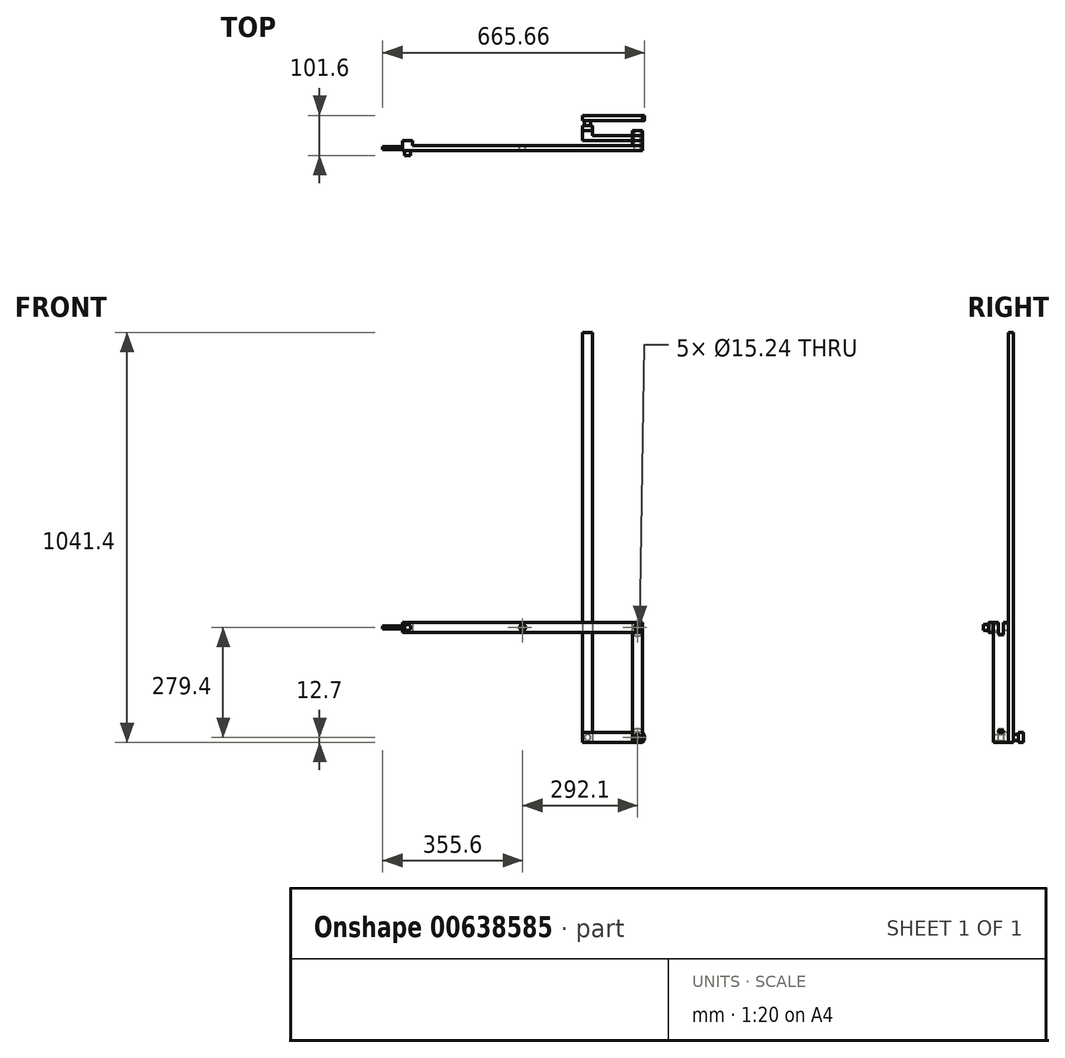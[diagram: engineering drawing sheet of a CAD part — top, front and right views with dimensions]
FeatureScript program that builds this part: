
annotation { "Feature Type Name" : "Feature", "Feature Type Description" : "" }
export const myFeature = defineFeature(function(context is Context, id is Id, definition is map)
    precondition{}
    {
        {
            var Q0;
            Q0=qCreatedBy(makeId("Front.planeOp"),FACE);
            var sketch = newSketch(context, id + "F0", { "sketchPlane" : qUnion([Q0])});
            skLineSegment(sketch, "E0.bottom", {"start": v(76.2, -12.7) * mm, "end": v(-76.2, -12.7) * mm});
            skLineSegment(sketch, "E0.top", {"start": v(76.2, 12.7) * mm, "end": v(-76.2, 12.7) * mm});
            skLineSegment(sketch, "E0.left", {"start": v(76.2, -12.7) * mm, "end": v(76.2, 12.7) * mm});
            skLineSegment(sketch, "E0.right", {"start": v(-76.2, -12.7) * mm, "end": v(-76.2, 12.7) * mm});
            skPoint(sketch, "E0.middle", {"position": v(0, 0) * mm});
            skCircle(sketch, "E1", {"center": v(-63.5, 0) * mm, "radius": 7.62 * mm});
            skLineSegment(sketch, "E2", {"start": v(-63.5, 0) * mm, "end": v(-63.5, 12.7) * mm, "construction": true});
            skLineSegment(sketch, "E3", {"start": v(-63.5, 0) * mm, "end": v(-76.2, 0) * mm, "construction": true});
            skCircle(sketch, "E4", {"center": v(63.5, 0) * mm, "radius": 7.62 * mm});
            skPoint(sketch, "E4.centerSnap0", {"position": v(76.2, 0) * mm});
            skLineSegment(sketch, "E5", {"start": v(63.5, 0) * mm, "end": v(76.2, 0) * mm, "construction": true});
            skSolve(sketch);
        }
        {
            var Q0;
            Q0=makeQuery(id+"F0.imprint","IMPRINT",FACE,{"disambiguationData":[TD([[makeQuery(id+"F0.imprint","IMPRINT",EDGE,{"derivedFrom":sQuery(id+"F0.wireOp",EDGE,"E0.bottom")}),-1.0]])]});
            extrude(context, id + "F1", {"entities" : qUnion([Q0]), "endBound" : BoundingType.SYMMETRIC, "depth" : 12.7 * mm, "offsetDistance" : 25.4 * mm});
        }
        {
            var Q0;
            Q0=makeQuery(id+"F1.opExtrude","CAP_FACE",FACE,{"disambiguationData":[OSD([sQuery(id+"F0.wireOp",EDGE,"E0.bottom"),sQuery(id+"F0.wireOp",EDGE,"E0.top"),sQuery(id+"F0.wireOp",EDGE,"E0.left"),sQuery(id+"F0.wireOp",EDGE,"E0.right"),sQuery(id+"F0.wireOp",EDGE,"E1"),sQuery(id+"F0.wireOp",EDGE,"E4")])],"isStart":false});
            var sketch = newSketch(context, id + "F2", { "sketchPlane" : qUnion([Q0])});
            skLineSegment(sketch, "E6.bottom", {"start": v(76.2, -12.7) * mm, "end": v(50.8, -12.7) * mm});
            skLineSegment(sketch, "E6.top", {"start": v(76.2, 292.1) * mm, "end": v(50.8, 292.1) * mm});
            skLineSegment(sketch, "E6.left", {"start": v(76.2, -12.7) * mm, "end": v(76.2, 292.1) * mm});
            skLineSegment(sketch, "E6.right", {"start": v(50.8, -12.7) * mm, "end": v(50.8, 292.1) * mm});
            skLineSegment(sketch, "E7", {"start": v(63.5, 0) * mm, "end": v(63.5, -12.7) * mm, "construction": true});
            skLineSegment(sketch, "E8", {"start": v(76.2, 139.7) * mm, "end": v(50.8, 139.7) * mm, "construction": true});
            skCircle(sketch, "E9", {"center": v(63.5, 279.4) * mm, "radius": 7.62 * mm});
            skLineSegment(sketch, "E10", {"start": v(76.2, 12.7) * mm, "end": v(50.8, 12.7) * mm});
            skSolve(sketch);
        }
        {
            var Q0;
            {var subQ2=sQuery(id+"F2.wireOp",EDGE,"E6.bottom");Q0=makeQuery(id+"F2.imprint","IMPRINT",FACE,{"disambiguationData":[TD([[makeQuery(id+"F2.imprint","IMPRINT",EDGE,{"derivedFrom":subQ2}),-1.0]])]});}
            var Q1;
            {var subQ1=sQuery(id+"F2.wireOp",EDGE,"E6.top");Q1=makeQuery(id+"F2.imprint","IMPRINT",FACE,{"disambiguationData":[TD([[makeQuery(id+"F2.imprint","IMPRINT",EDGE,{"derivedFrom":subQ1}),1.0]])]});}
            extrude(context, id + "F3", {"entities" : qUnion([Q0, Q1]), "depth" : 12.7 * mm, "offsetDistance" : 25.4 * mm});
        }
        {
            var Q0;
            {var subQ1=sQuery(id+"F2.wireOp",EDGE,"E6.top");Q0=makeQuery(id+"F2.imprint","IMPRINT",FACE,{"disambiguationData":[TD([[makeQuery(id+"F2.imprint","IMPRINT",EDGE,{"derivedFrom":subQ1}),1.0]])]});}
            var sketch = newSketch(context, id + "F4", { "sketchPlane" : qUnion([Q0])});
            skLineSegment(sketch, "E11.0", {"start": v(50.8, -12.7) * mm, "end": v(50.8, 292.1) * mm});
            skCircle(sketch, "E12.0", {"center": v(63.5, 0) * mm, "radius": 7.62 * mm});
            skCircle(sketch, "E13.0", {"center": v(63.5, 279.4) * mm, "radius": 7.62 * mm});
            skLineSegment(sketch, "E14", {"start": v(50.8, -12.7) * mm, "end": v(76.2, -12.7) * mm});
            skLineSegment(sketch, "E15.0", {"start": v(76.2, 292.1) * mm, "end": v(50.8, 292.1) * mm});
            skPoint(sketch, "E16.orphan", {"position": v(-76.2, 12.7) * mm});
            skLineSegment(sketch, "E17.trimOffspring", {"start": v(76.2, -12.7) * mm, "end": v(76.2, 292.1) * mm});
            skLineSegment(sketch, "E18", {"start": v(50.8, 139.7) * mm, "end": v(76.2, 139.7) * mm, "construction": true});
            skArc(sketch, "E19", {"start": v(50.8, 261.62) * mm, "mid": v(63.5, 257.55) * mm, "end": v(76.2, 261.62) * mm});
            skArc(sketch, "E20", {"start": v(76.2, 17.78) * mm, "mid": v(63.5, 21.85) * mm, "end": v(50.8, 17.78) * mm});
            skSolve(sketch);
        }
        {
            var Q0;
            {var subQ0=sQuery(id+"F4.wireOp",EDGE,"E19");Q0=makeQuery(id+"F4.imprint","IMPRINT",FACE,{"disambiguationData":[TD([[makeQuery(id+"F4.imprint","IMPRINT",EDGE,{"derivedFrom":subQ0}),-1.0]])]});}
            var Q1;
            Q1=makeQuery(id+"F1.opExtrude","CAP_FACE",FACE,{"disambiguationData":[OSD([sQuery(id+"F0.wireOp",EDGE,"E0.bottom"),sQuery(id+"F0.wireOp",EDGE,"E0.top"),sQuery(id+"F0.wireOp",EDGE,"E0.left"),sQuery(id+"F0.wireOp",EDGE,"E0.right"),sQuery(id+"F0.wireOp",EDGE,"E1"),sQuery(id+"F0.wireOp",EDGE,"E4")])],"isStart":true});
            extrude(context, id + "F5", {"entities" : qUnion([Q0]), "operationType" : NewBodyOperationType.ADD, "endBound" : BoundingType.UP_TO_SURFACE, "oppositeDirection" : true, "depth" : 34.04 * mm, "endBoundEntityFace" : qUnion([Q1]), "offsetDistance" : 25.4 * mm});
        }
        {
            var Q0;
            Q0=makeQuery(id+"F5.opExtrude","CAP_FACE",FACE,{"disambiguationData":[OSD([sQuery(id+"F4.wireOp",EDGE,"E11.0"),sQuery(id+"F4.wireOp",EDGE,"E17.trimOffspring"),sQuery(id+"F4.wireOp",EDGE,"E19"),sQuery(id+"F4.wireOp",EDGE,"E20")])],"isStart":false});
            var sketch = newSketch(context, id + "F6", { "sketchPlane" : qUnion([Q0])});
            skLineSegment(sketch, "E21.0", {"start": v(-50.8, -12.7) * mm, "end": v(-50.8, 292.1) * mm});
            skLineSegment(sketch, "E22.0", {"start": v(-76.2, -12.7) * mm, "end": v(-76.2, 292.1) * mm});
            skLineSegment(sketch, "E23.0", {"start": v(-76.2, 292.1) * mm, "end": v(-50.8, 292.1) * mm});
            skCircle(sketch, "E24.0", {"center": v(-63.5, 279.4) * mm, "radius": 7.62 * mm});
            skCircle(sketch, "E25.0", {"center": v(-63.5, 0) * mm, "radius": 7.62 * mm});
            skLineSegment(sketch, "E26.0", {"start": v(-76.2, -12.7) * mm, "end": v(-50.8, -12.7) * mm});
            skSolve(sketch);
        }
        {
            var Q0;
            {var subQ1=makeQuery(id+"F5.opExtrude","CAP_EDGE",EDGE,{"disambiguationData":[OSD([sQuery(id+"F4.wireOp",EDGE,"E19")])],"isStart":false});Q0=makeQuery(id+"F6.imprint","IMPRINT",FACE,{"disambiguationData":[TD([[makeQuery(id+"F6.imprint","IMPRINT",EDGE,{"derivedFrom":subQ1}),-1.0]])]});}
            var Q1;
            Q1=makeQuery(id+"F6.imprint","IMPRINT",FACE,{"disambiguationData":[TD([[makeQuery(id+"F6.imprint","IMPRINT",EDGE,{"derivedFrom":sQuery(id+"F6.wireOp",EDGE,"E25.0")}),-1.0]])]});
            var Q2;
            {var subQ0=sQuery(id+"F6.wireOp",EDGE,"E23.0");Q2=makeQuery(id+"F6.imprint","IMPRINT",FACE,{"disambiguationData":[TD([[makeQuery(id+"F6.imprint","IMPRINT",EDGE,{"derivedFrom":subQ0}),-1.0]])]});}
            extrude(context, id + "F7", {"entities" : qUnion([Q0, Q1, Q2]), "operationType" : NewBodyOperationType.ADD, "depth" : 12.7 * mm, "offsetDistance" : 25.4 * mm});
        }
        {
            var Q0;
            Q0=makeQuery(id+"F3.opExtrude","CAP_FACE",FACE,{"disambiguationData":[OSD([sQuery(id+"F0.wireOp",EDGE,"E4"),sQuery(id+"F2.wireOp",EDGE,"E6.bottom"),sQuery(id+"F2.wireOp",EDGE,"E6.top"),sQuery(id+"F2.wireOp",EDGE,"E6.left"),sQuery(id+"F2.wireOp",EDGE,"E6.right"),sQuery(id+"F2.wireOp",EDGE,"E9")])],"isStart":false});
            var sketch = newSketch(context, id + "F8", { "sketchPlane" : qUnion([Q0])});
            skLineSegment(sketch, "E27.bottom", {"start": v(76.2, 292.1) * mm, "end": v(-533.4, 292.1) * mm});
            skLineSegment(sketch, "E27.top", {"start": v(76.2, 266.7) * mm, "end": v(-533.4, 266.7) * mm});
            skLineSegment(sketch, "E27.left", {"start": v(76.2, 292.1) * mm, "end": v(76.2, 266.7) * mm});
            skLineSegment(sketch, "E27.right", {"start": v(-533.4, 292.1) * mm, "end": v(-533.4, 266.7) * mm});
            skCircle(sketch, "E28.0", {"center": v(63.5, 279.4) * mm, "radius": 7.62 * mm});
            skLineSegment(sketch, "E29", {"start": v(-228.6, 266.7) * mm, "end": v(-228.6, 292.1) * mm, "construction": true});
            skCircle(sketch, "E30", {"center": v(-520.7, 279.4) * mm, "radius": 7.62 * mm});
            skCircle(sketch, "E31", {"center": v(-228.6, 279.4) * mm, "radius": 7.62 * mm});
            skSolve(sketch);
        }
        {
            var Q0;
            {var subQ0=sQuery(id+"F8.wireOp",EDGE,"E27.right");Q0=makeQuery(id+"F8.imprint","IMPRINT",FACE,{"disambiguationData":[TD([[makeQuery(id+"F8.imprint","IMPRINT",EDGE,{"derivedFrom":subQ0}),1.0]])]});}
            var Q1;
            {var subQ0=sQuery(id+"F8.wireOp",EDGE,"E27.left");Q1=makeQuery(id+"F8.imprint","IMPRINT",FACE,{"disambiguationData":[TD([[makeQuery(id+"F8.imprint","IMPRINT",EDGE,{"derivedFrom":subQ0}),1.0]])]});}
            extrude(context, id + "F9", {"entities" : qUnion([Q0, Q1]), "depth" : 12.7 * mm, "offsetDistance" : 25.4 * mm});
        }
        {
            var Q0;
            Q0=makeQuery(id+"F1.opExtrude","CAP_FACE",FACE,{"disambiguationData":[OSD([sQuery(id+"F0.wireOp",EDGE,"E0.bottom"),sQuery(id+"F0.wireOp",EDGE,"E0.top"),sQuery(id+"F0.wireOp",EDGE,"E0.left"),sQuery(id+"F0.wireOp",EDGE,"E0.right"),sQuery(id+"F0.wireOp",EDGE,"E1"),sQuery(id+"F0.wireOp",EDGE,"E4")])],"isStart":true});
            var sketch = newSketch(context, id + "F10", { "sketchPlane" : qUnion([Q0])});
            skLineSegment(sketch, "E32.bottom", {"start": v(76.2, 12.7) * mm, "end": v(50.8, 12.7) * mm});
            skLineSegment(sketch, "E32.top", {"start": v(76.2, -12.7) * mm, "end": v(50.8, -12.7) * mm});
            skLineSegment(sketch, "E32.left", {"start": v(76.2, 12.7) * mm, "end": v(76.2, -12.7) * mm});
            skLineSegment(sketch, "E32.right", {"start": v(50.8, 12.7) * mm, "end": v(50.8, -12.7) * mm});
            skPoint(sketch, "E32.middle", {"position": v(63.5, 0) * mm});
            skCircle(sketch, "E33.0", {"center": v(63.5, 0) * mm, "radius": 7.62 * mm});
            skSolve(sketch);
        }
        {
            var Q0;
            Q0=makeQuery(id+"F10.imprint","IMPRINT",FACE,{"disambiguationData":[TD([[makeQuery(id+"F10.imprint","IMPRINT",EDGE,{"derivedFrom":sQuery(id+"F10.wireOp",EDGE,"E33.0")}),-1.0]])]});
            extrude(context, id + "F11", {"entities" : qUnion([Q0]), "oppositeDirection" : true, "depth" : 25.4 * mm, "offsetDistance" : 25.4 * mm});
        }
        {
            var Q0;
            Q0=makeQuery(id+"F10.imprint","IMPRINT",FACE,{"disambiguationData":[TD([[makeQuery(id+"F10.imprint","IMPRINT",EDGE,{"derivedFrom":sQuery(id+"F10.wireOp",EDGE,"E33.0")}),-1.0]])]});
            var Q1;
            Q1=makeQuery(id+"F10.imprint","IMPRINT",FACE,{"disambiguationData":[TD([[makeQuery(id+"F10.imprint","IMPRINT",EDGE,{"derivedFrom":sQuery(id+"F10.wireOp",EDGE,"E32.bottom")}),-1.0]])]});
            extrude(context, id + "F12", {"entities" : qUnion([Q0, Q1]), "operationType" : NewBodyOperationType.ADD, "depth" : 25.4 * mm, "offsetDistance" : 25.4 * mm});
        }
        {
            var Q0;
            Q0=makeQuery(id+"F12.opExtrude","SWEPT_FACE",FACE,{"disambiguationData":[OSD([sQuery(id+"F10.wireOp",EDGE,"E32.bottom")])]});
            var sketch = newSketch(context, id + "F13", { "sketchPlane" : qUnion([Q0])});
            skLineSegment(sketch, "E34", {"start": v(-76.2, 19.05) * mm, "end": v(-50.8, 19.05) * mm});
            skSolve(sketch);
        }
        {
            var Q0;
            {var subQ0=sQuery(id+"F13.wireOp",EDGE,"E34");Q0=makeQuery(id+"F13.imprint","IMPRINT",FACE,{"disambiguationData":[TD([[makeQuery(id+"F13.imprint","IMPRINT",EDGE,{"derivedFrom":subQ0}),1.0]])]});}
            extrude(context, id + "F14", {"entities" : qUnion([Q0]), "operationType" : NewBodyOperationType.ADD, "depth" : 889 * mm, "offsetDistance" : 25.4 * mm});
        }
        {
            var Q0;
            Q0=makeQuery(id+"F9.opExtrude","CAP_FACE",FACE,{"disambiguationData":[OSD([sQuery(id+"F8.wireOp",EDGE,"E27.bottom"),sQuery(id+"F8.wireOp",EDGE,"E27.top"),sQuery(id+"F8.wireOp",EDGE,"E27.left"),sQuery(id+"F8.wireOp",EDGE,"E27.right"),sQuery(id+"F8.wireOp",EDGE,"E28.0"),sQuery(id+"F8.wireOp",EDGE,"E30")])],"isStart":true});
            var sketch = newSketch(context, id + "F15", { "sketchPlane" : qUnion([Q0])});
            skLineSegment(sketch, "E35.bottom", {"start": v(533.4, 292.1) * mm, "end": v(508, 292.1) * mm});
            skLineSegment(sketch, "E35.top", {"start": v(533.4, 266.7) * mm, "end": v(508, 266.7) * mm});
            skLineSegment(sketch, "E35.left", {"start": v(533.4, 292.1) * mm, "end": v(533.4, 266.7) * mm});
            skLineSegment(sketch, "E35.right", {"start": v(508, 292.1) * mm, "end": v(508, 266.7) * mm});
            skPoint(sketch, "E35.middle", {"position": v(520.7, 279.4) * mm});
            skCircle(sketch, "E36.0", {"center": v(520.7, 279.4) * mm, "radius": 7.62 * mm});
            skSolve(sketch);
        }
        {
            var Q0;
            Q0=makeQuery(id+"F15.imprint","IMPRINT",FACE,{"disambiguationData":[TD([[makeQuery(id+"F15.imprint","IMPRINT",EDGE,{"derivedFrom":sQuery(id+"F15.wireOp",EDGE,"E36.0")}),-1.0]])]});
            var Q1;
            Q1=makeQuery(id+"F15.imprint","IMPRINT",FACE,{"disambiguationData":[TD([[makeQuery(id+"F15.imprint","IMPRINT",EDGE,{"derivedFrom":sQuery(id+"F15.wireOp",EDGE,"E35.bottom")}),-1.0]])]});
            extrude(context, id + "F16", {"entities" : qUnion([Q0, Q1]), "depth" : 12.7 * mm, "offsetDistance" : 25.4 * mm});
        }
        {
            var Q0;
            Q0=makeQuery(id+"F15.imprint","IMPRINT",FACE,{"disambiguationData":[TD([[makeQuery(id+"F15.imprint","IMPRINT",EDGE,{"derivedFrom":sQuery(id+"F15.wireOp",EDGE,"E36.0")}),-1.0]])]});
            extrude(context, id + "F17", {"entities" : qUnion([Q0]), "operationType" : NewBodyOperationType.ADD, "oppositeDirection" : true, "depth" : 25.4 * mm, "offsetDistance" : 25.4 * mm});
        }
        {
            var Q0;
            Q0=makeQuery(id+"F14.opExtrude","CAP_FACE",FACE,{"disambiguationData":[OSD([sQuery(id+"F0.wireOp",EDGE,"E0.top"),sQuery(id+"F10.wireOp",EDGE,"E32.bottom"),sQuery(id+"F10.wireOp",EDGE,"E32.left"),sQuery(id+"F10.wireOp",EDGE,"E32.right"),sQuery(id+"F13.wireOp",EDGE,"E34")])],"isStart":false});
            extrude(context, id + "F18", {"entities" : qUnion([Q0]), "operationType" : NewBodyOperationType.ADD, "depth" : 127 * mm, "offsetDistance" : 25.4 * mm});
        }
        {
            var Q0;
            Q0=makeQuery(id+"F9.opExtrude","SWEPT_FACE",FACE,{"disambiguationData":[OSD([sQuery(id+"F8.wireOp",EDGE,"E27.right")])]});
            var sketch = newSketch(context, id + "F19", { "sketchPlane" : qUnion([Q0])});
            skCircle(sketch, "E37", {"center": v(25.4, 279.4) * mm, "radius": 3.81 * mm});
            skPoint(sketch, "E37.centerSnap0", {"position": v(31.75, 279.4) * mm});
            skPoint(sketch, "E37.centerSnap1", {"position": v(25.4, 292.1) * mm});
            skSolve(sketch);
        }
        {
            var Q0;
            Q0=makeQuery(id+"F19.imprint","IMPRINT",FACE,{"disambiguationData":[TD([[makeQuery(id+"F19.imprint","IMPRINT",EDGE,{"derivedFrom":sQuery(id+"F19.wireOp",EDGE,"E37")}),1.0]])]});
            extrude(context, id + "F20", {"entities" : qUnion([Q0]), "operationType" : NewBodyOperationType.ADD, "depth" : 50.8 * mm, "offsetDistance" : 25.4 * mm});
        }
        {
            var Q0;
            Q0=makeQuery(id+"F11.opExtrude","CAP_FACE",FACE,{"disambiguationData":[OSD([sQuery(id+"F10.wireOp",EDGE,"E33.0")])],"isStart":false});
            extrude(context, id + "F21", {"entities" : qUnion([Q0]), "operationType" : NewBodyOperationType.REMOVE, "oppositeDirection" : true, "depth" : 65.02 * mm, "offsetDistance" : 25.4 * mm});
        }
        {
            var Q0;
            Q0=makeQuery(id+"F1.opExtrude","CAP_FACE",FACE,{"disambiguationData":[OSD([sQuery(id+"F0.wireOp",EDGE,"E0.bottom"),sQuery(id+"F0.wireOp",EDGE,"E0.top"),sQuery(id+"F0.wireOp",EDGE,"E0.left"),sQuery(id+"F0.wireOp",EDGE,"E0.right"),sQuery(id+"F0.wireOp",EDGE,"E1"),sQuery(id+"F0.wireOp",EDGE,"E4")])],"isStart":false});
            var sketch = newSketch(context, id + "F22", { "sketchPlane" : qUnion([Q0])});
            skCircle(sketch, "E38.0", {"center": v(-63.5, 0) * mm, "radius": 7.62 * mm});
            skSolve(sketch);
        }
        {
            var Q0;
            Q0=makeQuery(id+"F22.imprint","IMPRINT",FACE,{"disambiguationData":[TD([[makeQuery(id+"F22.imprint","IMPRINT",EDGE,{"derivedFrom":sQuery(id+"F22.wireOp",EDGE,"E38.0")}),1.0]])]});
            extrude(context, id + "F23", {"entities" : qUnion([Q0]), "operationType" : NewBodyOperationType.ADD, "oppositeDirection" : true, "depth" : 50.8 * mm, "offsetDistance" : 25.4 * mm});
        }
        {
            var Q0;
            Q0=makeQuery(id+"F23.opExtrude","CAP_FACE",FACE,{"disambiguationData":[OSD([sQuery(id+"F22.wireOp",EDGE,"E38.0")])],"isStart":false});
            var sketch = newSketch(context, id + "F24", { "sketchPlane" : qUnion([Q0])});
            skLineSegment(sketch, "E39.0", {"start": v(-76.2, 12.7) * mm, "end": v(76.2, 12.7) * mm});
            skLineSegment(sketch, "E40.0", {"start": v(-76.2, -12.7) * mm, "end": v(76.2, -12.7) * mm});
            skLineSegment(sketch, "E41.0", {"start": v(76.2, -12.7) * mm, "end": v(76.2, 12.7) * mm});
            skCircle(sketch, "E42.0", {"center": v(-63.5, 0) * mm, "radius": 7.62 * mm, "construction": true});
            skArc(sketch, "E43", {"start": v(-76.2, 12.7) * mm, "mid": v(-81.46, 0) * mm, "end": v(-76.2, -12.7) * mm});
            skPoint(sketch, "E44.orphan", {"position": v(-76.2, 0) * mm});
            skPoint(sketch, "E45.orphan", {"position": v(76.2, 0) * mm});
            skSolve(sketch);
        }
        {
            var Q0;
            Q0=makeQuery(id+"F24.imprint","IMPRINT",FACE,{"disambiguationData":[TD([[makeQuery(id+"F24.imprint","IMPRINT",EDGE,{"derivedFrom":sQuery(id+"F24.wireOp",EDGE,"E39.0")}),-1.0]])]});
            var Q1;
            Q1=makeQuery(id+"F24.imprint","IMPRINT",FACE,{"disambiguationData":[TD([[makeQuery(id+"F24.imprint","IMPRINT",EDGE,{"derivedFrom":makeQuery(id+"F23.opExtrude","CAP_EDGE",EDGE,{"disambiguationData":[OSD([sQuery(id+"F22.wireOp",EDGE,"E38.0")])],"isStart":false})}),-1.0]])]});
            extrude(context, id + "F25", {"entities" : qUnion([Q0, Q1]), "operationType" : NewBodyOperationType.ADD, "depth" : 12.7 * mm, "offsetDistance" : 25.4 * mm});
        }
    });
